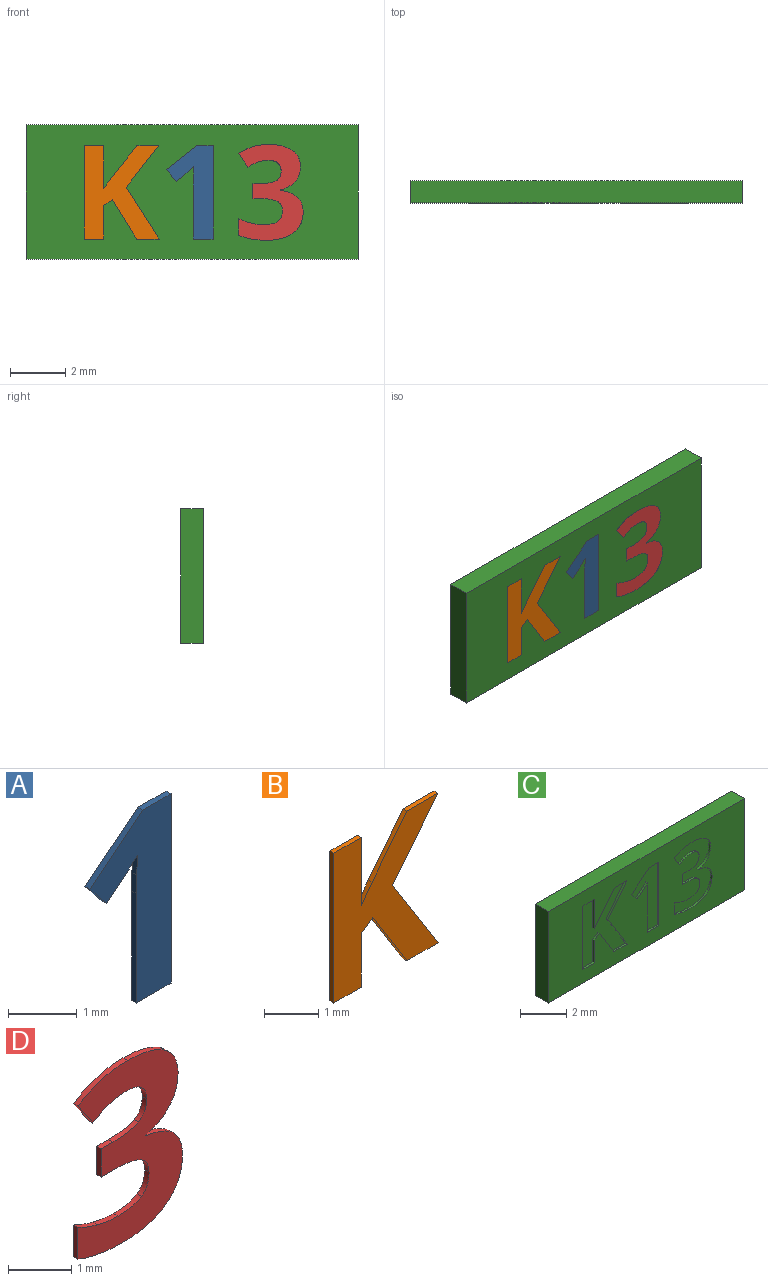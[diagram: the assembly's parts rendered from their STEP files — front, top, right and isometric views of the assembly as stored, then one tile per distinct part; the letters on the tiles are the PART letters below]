
ASSEMBLY  parts=4 mates=3
PART A: 12 faces, bbox 1.7x0.1x3.4 mm
  f0: plane 3.37x1.67mm, normal (0,-1,0), area 2.9mm2, adj f1,f2,f3,f4,f5,f6,f7,f9
  f1: plane 0.59x0.1mm, normal (0,0,1), area 0.1mm2, adj f0,f2,f8,f10
  f2: plane 1.09x0.86mm, normal (-0.62,0,0.78), area 0.1mm2, adj f0,f1,f3,f8
  f3: plane 0.43x0.34mm, normal (-0.78,0,-0.63), area 0.1mm2, adj f0,f2,f4,f8
  f4: plane 0.39x0.31mm, normal (0.63,0,-0.78), area 0mm2, adj f0,f3,f5,f8
  f5: extruded ~0.25x0.23mm, area 0mm2, adj f0,f4,f6,f8
  f6: plane 0.35x0.1mm, normal (-1,0,0.03), area 0mm2, adj f0,f5,f7,f8
  f7: plane 0.32x0.1mm, normal (-1,0,0.02), area 0mm2, adj f0,f6,f8,f9
  f8: plane 3.37x1.67mm, normal (0,1,0), area 2.9mm2, adj f1,f2,f3,f4,f5,f6,f7,f9
  f9: plane 1.95x0.1mm, normal (-1,0,0), area 0.2mm2, adj f0,f7,f8,f11
  f10: plane 3.37x0.1mm, normal (1,0,0), area 0.3mm2, adj f0,f1,f8,f11
  f11: plane 0.71x0.1mm, normal (0,0,-1), area 0.1mm2, adj f0,f8,f9,f10
PART B: 15 faces, bbox 2.7x0.1x3.4 mm
  f0: plane 3.37x2.71mm, normal (0,-1,0), area 5.2mm2, adj f1,f2,f3,f4,f5,f6,f7,f8
  f1: plane 1.49x1.18mm, normal (0.79,0,-0.62), area 0.2mm2, adj f0,f2,f11,f13
  f2: plane 0.79x0.1mm, normal (0,0,1), area 0.1mm2, adj f0,f1,f3,f11
  f3: plane 1.15x0.91mm, normal (-0.78,0,0.62), area 0.1mm2, adj f0,f2,f4,f11
  f4: plane 0.4x0.28mm, normal (-0.82,0,0.58), area 0mm2, adj f0,f3,f5,f11
  f5: plane 1.54x0.1mm, normal (1,0,0), area 0.2mm2, adj f0,f4,f6,f11
  f6: plane 0.72x0.1mm, normal (0,0,1), area 0.1mm2, adj f0,f5,f7,f11
  f7: plane 3.37x0.1mm, normal (-1,0,0), area 0.3mm2, adj f0,f6,f8,f11
  f8: plane 0.72x0.1mm, normal (0,0,-1), area 0.1mm2, adj f0,f7,f9,f11
  f9: plane 1.2x0.1mm, normal (1,0,0), area 0.1mm2, adj f0,f8,f10,f11
  f10: plane 0.3x0.22mm, normal (0.58,0,-0.81), area 0mm2, adj f0,f9,f11,f12
  f11: plane 3.37x2.71mm, normal (0,1,0), area 5.2mm2, adj f1,f2,f3,f4,f5,f6,f7,f8
  f12: plane 1.42x0.88mm, normal (-0.85,0,-0.53), area 0.2mm2, adj f0,f10,f11,f14
  f13: plane 1.88x1.19mm, normal (0.85,0,0.53), area 0.2mm2, adj f0,f1,f11,f14
  f14: plane 0.81x0.1mm, normal (0,0,-1), area 0.1mm2, adj f0,f11,f12,f13
PART C: 59 faces, bbox 12x0.8x4.9 mm
  f0: plane 12x4.85mm, normal (0,-1,0), area 45.8mm2, adj f1,f2,f3,f4,f6,f7,f8,f9
  f1: plane 12x0.8mm, normal (0,0,-1), area 9.6mm2, adj f0,f2,f4,f5
  f2: plane 4.85x0.8mm, normal (1,0,0), area 3.9mm2, adj f0,f1,f3,f5
  f3: plane 12x0.8mm, normal (0,0,1), area 9.6mm2, adj f0,f2,f4,f5
  f4: plane 4.85x0.8mm, normal (-1,0,0), area 3.9mm2, adj f0,f1,f3,f5
  f5: plane 12x4.85mm, normal (0,1,0), area 58.2mm2, adj f1,f2,f3,f4
  f6: extruded ~0.59x0.3mm, area 0.1mm2, adj f0,f7,f32,f33
  f7: extruded ~0.83x0.21mm, area 0.1mm2, adj f0,f6,f8,f33
  f8: extruded ~1.1x0.33mm, area 0.1mm2, adj f0,f7,f9,f33
  f9: plane 0.49x0.33mm, normal (0.83,0,0.56), area 0.1mm2, adj f0,f8,f10,f33
  f10: extruded ~0.38x0.19mm, area 0mm2, adj f0,f9,f11,f33
  f11: extruded ~0.34x0.1mm, area 0mm2, adj f0,f10,f12,f33
  f12: extruded ~0.48x0.38mm, area 0.1mm2, adj f0,f11,f13,f33
  f13: extruded ~0.35x0.18mm, area 0mm2, adj f0,f12,f14,f33
  f14: extruded ~0.57x0.1mm, area 0.1mm2, adj f0,f13,f15,f33
  f15: plane 0.26x0.1mm, normal (0,0,-1), area 0mm2, adj f0,f14,f16,f33
  f16: plane 0.55x0.1mm, normal (1,0,0), area 0.1mm2, adj f0,f15,f17,f33
  f17: plane 0.26x0.1mm, normal (0,0,1), area 0mm2, adj f0,f16,f18,f33
  f18: extruded ~0.62x0.1mm, area 0.1mm2, adj f0,f17,f19,f33
  f19: extruded ~0.34x0.19mm, area 0mm2, adj f0,f18,f20,f33
  f20: extruded ~0.39x0.17mm, area 0mm2, adj f0,f19,f21,f33
  f21: extruded ~0.52x0.12mm, area 0.1mm2, adj f0,f20,f22,f33
  f22: extruded ~0.47x0.1mm, area 0mm2, adj f0,f21,f23,f33
  f23: extruded ~0.43x0.16mm, area 0mm2, adj f0,f22,f24,f33
  f24: plane 0.61x0.1mm, normal (1,0,0), area 0.1mm2, adj f0,f23,f25,f33
  f25: extruded ~0.97x0.18mm, area 0.1mm2, adj f0,f24,f26,f33
  f26: extruded ~1.01x0.27mm, area 0.1mm2, adj f0,f25,f27,f33
  f27: extruded ~0.76x0.35mm, area 0.1mm2, adj f0,f26,f28,f33
  f28: extruded ~0.53x0.21mm, area 0.1mm2, adj f0,f27,f29,f33
  f29: extruded ~0.62x0.25mm, area 0.1mm2, adj f0,f28,f30,f33
  f30: plane 0.1x0.01mm, normal (-1,0,0), area 0mm2, adj f0,f29,f31,f33
  f31: extruded ~0.54x0.3mm, area 0.1mm2, adj f0,f30,f32,f33
  f32: extruded ~0.54x0.19mm, area 0.1mm2, adj f0,f6,f31,f33
  f33: plane 3.47x2.33mm, normal (0,-1,0), area 4.3mm2, adj f6,f7,f8,f9,f10,f11,f12,f13
  f34: plane 3.37x0.1mm, normal (-1,0,0), area 0.3mm2, adj f0,f35,f43,f44
  f35: plane 0.59x0.1mm, normal (0,0,-1), area 0.1mm2, adj f0,f34,f36,f44
  f36: plane 1.09x0.86mm, normal (0.62,0,-0.78), area 0.1mm2, adj f0,f35,f37,f44
  f37: plane 0.43x0.34mm, normal (0.78,0,0.63), area 0.1mm2, adj f0,f36,f38,f44
  f38: plane 0.39x0.31mm, normal (-0.63,0,0.78), area 0mm2, adj f0,f37,f39,f44
  f39: extruded ~0.25x0.23mm, area 0mm2, adj f0,f38,f40,f44
  f40: plane 0.35x0.1mm, normal (1,0,-0.03), area 0mm2, adj f0,f39,f41,f44
  f41: plane 0.32x0.1mm, normal (1,0,-0.02), area 0mm2, adj f0,f40,f42,f44
  f42: plane 1.95x0.1mm, normal (1,0,0), area 0.2mm2, adj f0,f41,f43,f44
  f43: plane 0.71x0.1mm, normal (0,0,1), area 0.1mm2, adj f0,f34,f42,f44
  f44: plane 3.37x1.67mm, normal (0,-1,0), area 2.9mm2, adj f34,f35,f36,f37,f38,f39,f40,f41
  f45: plane 1.88x1.19mm, normal (-0.85,0,-0.53), area 0.2mm2, adj f0,f46,f57,f58
  f46: plane 1.49x1.18mm, normal (-0.79,0,0.62), area 0.2mm2, adj f0,f45,f47,f58
  f47: plane 0.79x0.1mm, normal (0,0,-1), area 0.1mm2, adj f0,f46,f48,f58
  f48: plane 1.15x0.91mm, normal (0.78,0,-0.62), area 0.1mm2, adj f0,f47,f49,f58
  f49: plane 0.4x0.28mm, normal (0.82,0,-0.58), area 0mm2, adj f0,f48,f50,f58
  f50: plane 1.54x0.1mm, normal (-1,0,0), area 0.2mm2, adj f0,f49,f51,f58
  f51: plane 0.72x0.1mm, normal (0,0,-1), area 0.1mm2, adj f0,f50,f52,f58
  f52: plane 3.37x0.1mm, normal (1,0,0), area 0.3mm2, adj f0,f51,f53,f58
  f53: plane 0.72x0.1mm, normal (0,0,1), area 0.1mm2, adj f0,f52,f54,f58
  f54: plane 1.2x0.1mm, normal (-1,0,0), area 0.1mm2, adj f0,f53,f55,f58
  f55: plane 0.3x0.22mm, normal (-0.58,0,0.81), area 0mm2, adj f0,f54,f56,f58
  f56: plane 1.42x0.88mm, normal (0.85,0,0.53), area 0.2mm2, adj f0,f55,f57,f58
  f57: plane 0.81x0.1mm, normal (0,0,1), area 0.1mm2, adj f0,f45,f56,f58
  f58: plane 3.37x2.71mm, normal (0,-1,0), area 5.2mm2, adj f45,f46,f47,f48,f49,f50,f51,f52
PART D: 29 faces, bbox 2.3x0.1x3.5 mm
  f0: plane 3.47x2.33mm, normal (0,-1,0), area 4.3mm2, adj f1,f2,f3,f4,f5,f6,f7,f8
  f1: extruded ~0.83x0.21mm, area 0.1mm2, adj f0,f2,f25,f27
  f2: extruded ~1.1x0.33mm, area 0.1mm2, adj f0,f1,f3,f25
  f3: plane 0.49x0.33mm, normal (-0.83,0,-0.56), area 0.1mm2, adj f0,f2,f4,f25
  f4: extruded ~0.38x0.19mm, area 0mm2, adj f0,f3,f5,f25
  f5: extruded ~0.34x0.1mm, area 0mm2, adj f0,f4,f6,f25
  f6: extruded ~0.48x0.38mm, area 0.1mm2, adj f0,f5,f7,f25
  f7: extruded ~0.35x0.18mm, area 0mm2, adj f0,f6,f8,f25
  f8: extruded ~0.57x0.1mm, area 0.1mm2, adj f0,f7,f9,f25
  f9: plane 0.26x0.1mm, normal (0,0,1), area 0mm2, adj f0,f8,f10,f25
  f10: plane 0.55x0.1mm, normal (-1,0,0), area 0.1mm2, adj f0,f9,f11,f25
  f11: plane 0.26x0.1mm, normal (0,0,-1), area 0mm2, adj f0,f10,f12,f25
  f12: extruded ~0.62x0.1mm, area 0.1mm2, adj f0,f11,f13,f25
  f13: extruded ~0.34x0.19mm, area 0mm2, adj f0,f12,f14,f25
  f14: extruded ~0.39x0.17mm, area 0mm2, adj f0,f13,f15,f25
  f15: extruded ~0.52x0.12mm, area 0.1mm2, adj f0,f14,f16,f25
  f16: extruded ~0.47x0.1mm, area 0mm2, adj f0,f15,f17,f25
  f17: extruded ~0.43x0.16mm, area 0mm2, adj f0,f16,f18,f25
  f18: plane 0.61x0.1mm, normal (-1,0,0), area 0.1mm2, adj f0,f17,f19,f25
  f19: extruded ~0.97x0.18mm, area 0.1mm2, adj f0,f18,f20,f25
  f20: extruded ~1.01x0.27mm, area 0.1mm2, adj f0,f19,f21,f25
  f21: extruded ~0.76x0.35mm, area 0.1mm2, adj f0,f20,f22,f25
  f22: extruded ~0.53x0.21mm, area 0.1mm2, adj f0,f21,f23,f25
  f23: extruded ~0.62x0.25mm, area 0.1mm2, adj f0,f22,f24,f25
  f24: plane 0.1x0.01mm, normal (1,0,0), area 0mm2, adj f0,f23,f25,f26
  f25: plane 3.47x2.33mm, normal (0,1,0), area 4.3mm2, adj f1,f2,f3,f4,f5,f6,f7,f8
  f26: extruded ~0.54x0.3mm, area 0.1mm2, adj f0,f24,f25,f28
  f27: extruded ~0.59x0.3mm, area 0.1mm2, adj f0,f1,f25,f28
  f28: extruded ~0.54x0.19mm, area 0.1mm2, adj f0,f25,f26,f27
PLACE A t=(-1.64,0.4,-0.01)mm
PLACE B t=(-1.64,0.4,-0.01)mm
PLACE C t=(-0.01,0.4,-0.01)mm
PLACE D t=(1.34,0.4,-0.01)mm
MATE fastened D.f0 <-> C.f0  axis (0,-1,0) through (1.68,-0.4,-1.58)mm
MATE fastened A.f0 <-> C.f0  axis (0,-1,0) through (0.04,-0.4,-1.71)mm
MATE fastened B.f0 <-> C.f0  axis (0,-1,0) through (-3.91,-0.4,-1.71)mm
